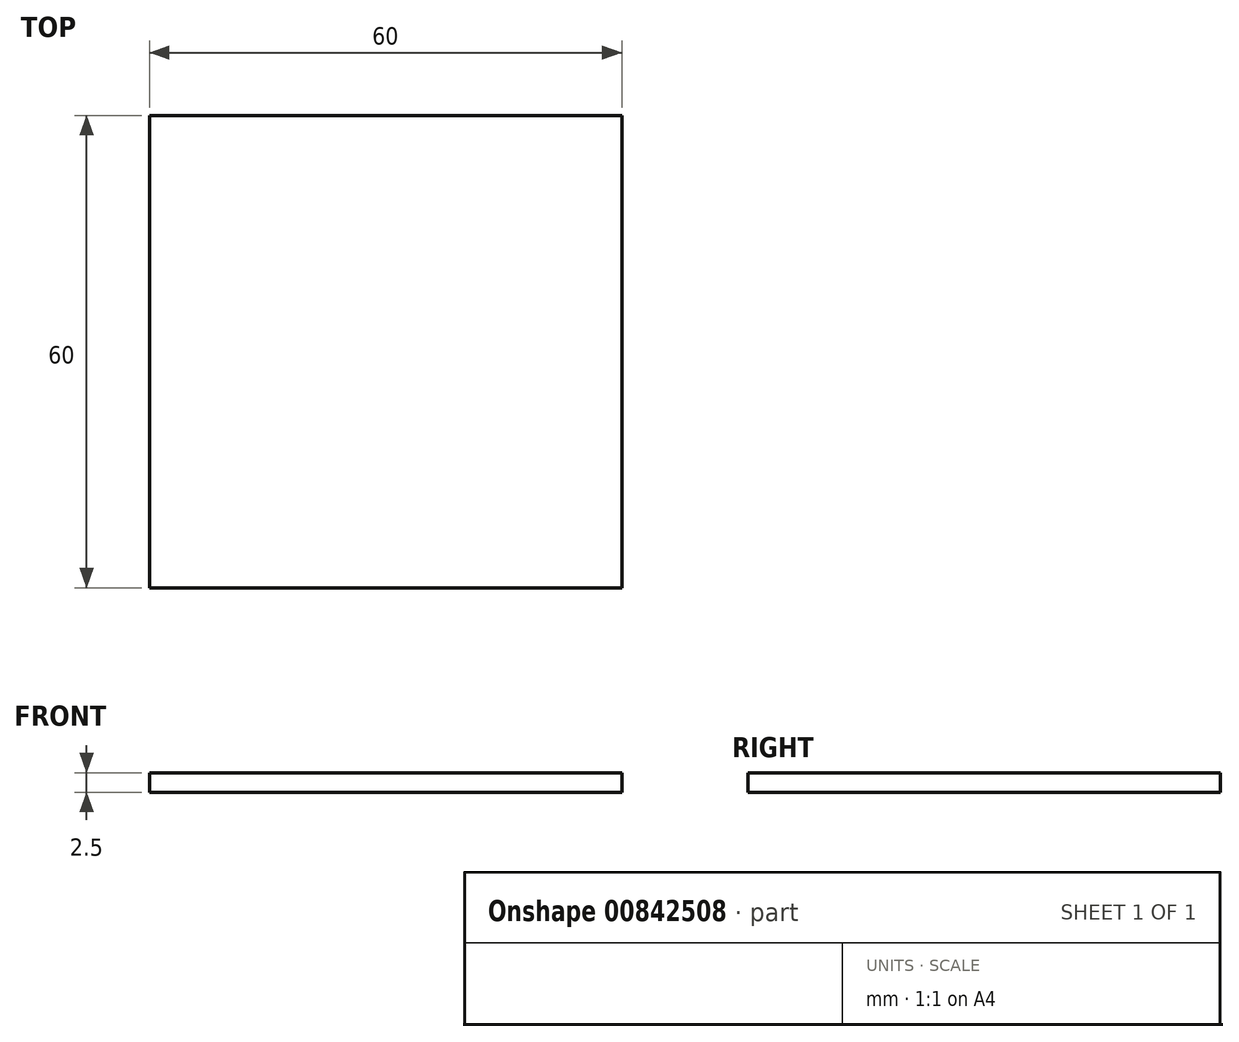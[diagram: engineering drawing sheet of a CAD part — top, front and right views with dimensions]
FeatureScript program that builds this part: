
annotation { "Feature Type Name" : "Feature", "Feature Type Description" : "" }
export const myFeature = defineFeature(function(context is Context, id is Id, definition is map)
    precondition{}
    {
        {
            var Q0;
            Q0=qCreatedBy(makeId("Top.planeOp"),FACE);
            var sketch = newSketch(context, id + "F0", { "sketchPlane" : qUnion([Q0])});
            skLineSegment(sketch, "E0.bottom", {"start": v(0, 0) * mm, "end": v(60, 0) * mm});
            skLineSegment(sketch, "E0.top", {"start": v(0, 60) * mm, "end": v(60, 60) * mm});
            skLineSegment(sketch, "E0.left", {"start": v(0, 0) * mm, "end": v(0, 60) * mm});
            skLineSegment(sketch, "E0.right", {"start": v(60, 0) * mm, "end": v(60, 60) * mm});
            skSolve(sketch);
        }
        {
            var Q0;
            Q0 = qSketchRegion(id + "F0", true);
            extrude(context, id + "F1", {"entities" : qUnion([Q0]), "depth" : 2.5 * mm, "offsetDistance" : 25 * mm});
        }
    });
